# Revit family: Trim_Set-GROHE-Defined-29301-Series
name_source: partatom
category: Plumbing Fixtures
units: mm (PartAtom-declared; Revit-internal decimal feet)

## family parameters
Cut with Voids When Loaded = No
Host = Face
OmniClass Number = 23.45.05.14.17
OmniClass Title = Showers
Part Type = Normal
Room Calculation Point = No
Round Connector Dimension = Use Diameter
Shared = Yes

## types (2) — shared parameters
48346000 Spindle Extension = No
6554100M Fixing Clamp = No
ADA Compliant = Yes
Assembly Code = D2010710
CW Connection = Yes
CWFU = 3
Cold Water Connection Diameter = 1/2"
Cold Water Connection Radius = 1/4"
Compliance Certifications = • ADA• Low Lead Certified• CSA B125.1• ASME A112.18.1• Complies with lead plumbing laws
Connection From Wall front To Central of pipe = 2 1/8"
Default Elevation = 44"
HW Connection = Yes
HWFU = 3
Hand Shower Connection = Yes
Hand Shower Connection Description = 1/2'' NPT Global Hand Shower Outlet
Hand Shower Tempered Connection Diameter = 1/2"
Height = 5 1/16"
Hot Water Connection Diameter = 1"
Hot Water Connection Radius = 1/4"
Installation Type = Wall Mounted
Length = 2 3/8"
Manufacturer = Grohe
Product Documentation Link = https://americanstandard.box.com
Product Page URL = https://www.grohe.us
Revised Date = 06/06/2023
Shower Connection = Yes
Shower Connection Description = 1/2'' NPT Global Shower Outlet
Shower Tempered Connection Diameter = 1/2"
Spout Connection = Yes
Spout Connection Description = 1/2'' NPT Global Spout Outlet
Spout Tempered Connection Diameter = 1/2"
Tempered Water Connection = Yes
URL = https://www.grohe.us
Vent Connection = No
Warranty Information = Limited lifetime warranty
Waste Connection = No
Width = 3 1/16"
cUPC Compliant = Yes
zero-valued in all types: WFU

## per-type parameters (varying)
| type | Description | Finish | Material |
| 29301000 | DEFINED 3-Way Diverter Trim Starlight Chrome | Metal-Grohe-000-Starlight Chrome | Metal-Grohe-000-Starlight Chrome |
| 29301EN0 | DEFINED 3-Way Diverter Trim Brushed Nickel | Metal-Grohe-EN0-Brushed Nickel | Metal-Grohe-EN0-Brushed Nickel |

note: column(s) folded — value = type name in every type: Model

## geometry (parser evidence)
native form markers: Sweep x5
no freeform markers — native parametric forms only
